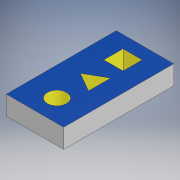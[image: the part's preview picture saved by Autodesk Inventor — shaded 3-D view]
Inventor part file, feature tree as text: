
AUTODESK INVENTOR PART (.ipt)
format: ipt  version: 2018 (Build 220112000, 112)  size: 131,072 bytes
history: native  units: in
note: dims shown in document units (in); Inventor stores cm internally (conversion verified against a paired STEP export)
features: extrude x4, sketch x4
ambient origin geometry x8: Origin, YZ Plane, XZ Plane, XY Plane, X Axis, Y Axis, Z Axis, Center Point
bodies: Solid1 (feature_tree)
feature tree (8):
  extrude  "Extrusion1"  Depth=3.0in
  extrude  "Extrusion2"  Depth=1.0in
  extrude  "Extrusion3"  Depth=1.149in
  extrude  "Extrusion4"  Depth=1.0in
  sketch  "Sketch1"  dims[d0=5.75in d1=3.0in]
  sketch  "Sketch2"  dims[d2=1.0in d3=0.0in d4=1.0in]
  sketch  "Sketch3"  dims[d5=1.5in d6=1.149in]
  sketch  "Sketch4"  dims[d7=1.0in d8=0.0in d9=1.0in d10=0.649in d11=1.0in d12=1.0in d13=0.0in d14=1.0in d15=1.154in d16=2.298in d17=1.0in d18=1.0in d19=0.0in]
